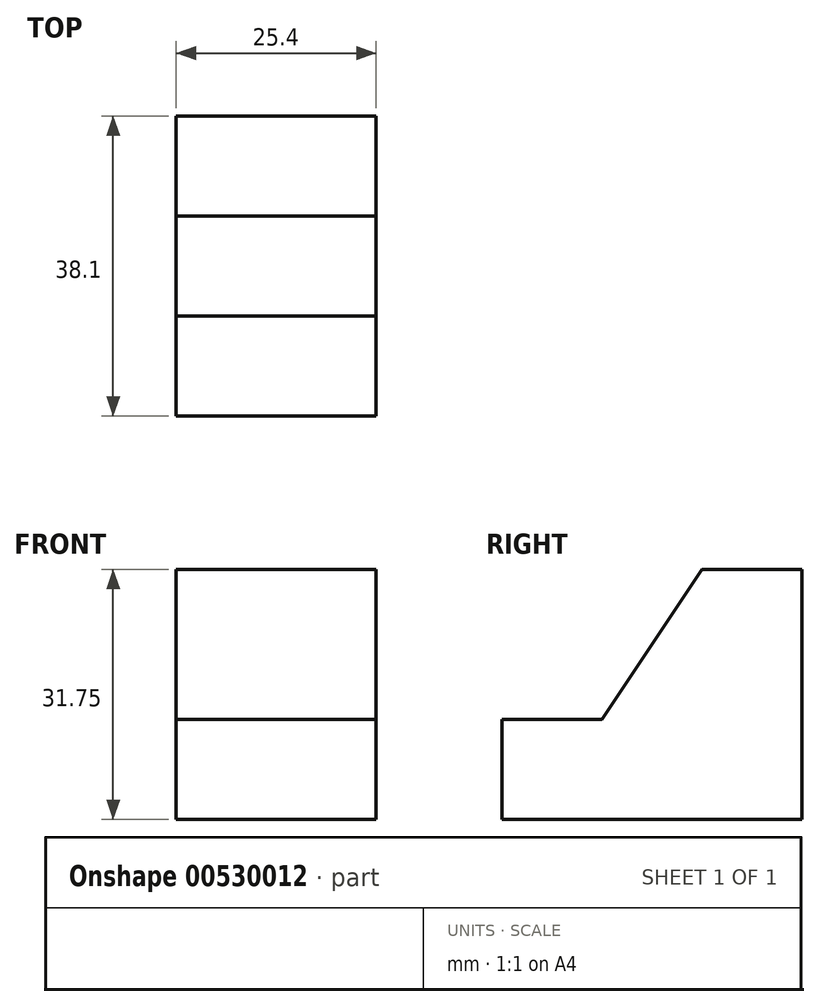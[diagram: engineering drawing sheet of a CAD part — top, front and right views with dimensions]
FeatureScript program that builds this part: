
annotation { "Feature Type Name" : "Feature", "Feature Type Description" : "" }
export const myFeature = defineFeature(function(context is Context, id is Id, definition is map)
    precondition{}
    {
        {
            var Q0;
            Q0=qCreatedBy(makeId("Right.planeOp"),FACE);
            var sketch = newSketch(context, id + "F0", { "sketchPlane" : qUnion([Q0])});
            skLineSegment(sketch, "E0", {"start": v(55.08, 43.57) * mm, "end": v(55.08, 11.82) * mm});
            skLineSegment(sketch, "E1", {"start": v(55.08, 11.82) * mm, "end": v(16.98, 11.82) * mm});
            skLineSegment(sketch, "E2", {"start": v(16.98, 11.82) * mm, "end": v(16.98, 24.52) * mm});
            skLineSegment(sketch, "E3", {"start": v(16.98, 24.52) * mm, "end": v(29.68, 24.52) * mm});
            skLineSegment(sketch, "E4", {"start": v(55.08, 43.57) * mm, "end": v(42.38, 43.57) * mm});
            skLineSegment(sketch, "E5", {"start": v(42.38, 43.57) * mm, "end": v(29.68, 24.52) * mm});
            skSolve(sketch);
        }
        {
            var Q0;
            Q0=makeQuery(id+"F0.imprint","IMPRINT",FACE,{"disambiguationData":[TD([[makeQuery(id+"F0.imprint","IMPRINT",EDGE,{"derivedFrom":sQuery(id+"F0.wireOp",EDGE,"E0")}),-1.0]])]});
            extrude(context, id + "F1", {"entities" : qUnion([Q0]), "depth" : 25.4 * mm, "offsetDistance" : 25.4 * mm});
        }
    });
